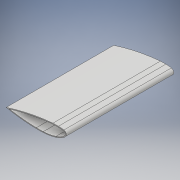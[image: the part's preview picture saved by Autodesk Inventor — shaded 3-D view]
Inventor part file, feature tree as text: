
AUTODESK INVENTOR PART (.ipt)
format: ipt  version: 2018.2 (Build 222227000, 227)  size: 133,120 bytes
history: native  units: mm
features: extrude x1, shell x1, sketch x1, projected_geometry x1
ambient origin geometry x8: Origin, YZ Plane, XZ Plane, XY Plane, X Axis, Y Axis, Z Axis, Center Point
bodies: Body1 (feature_tree)
feature tree (4):
  extrude  "押し出し1"  Depth=394.0mm TaperAngle=0.0deg
  shell  "シェル1"  Thickness=3.0mm
  sketch  "スケッチ1"
  projected_geometry  "投影ループ1"
